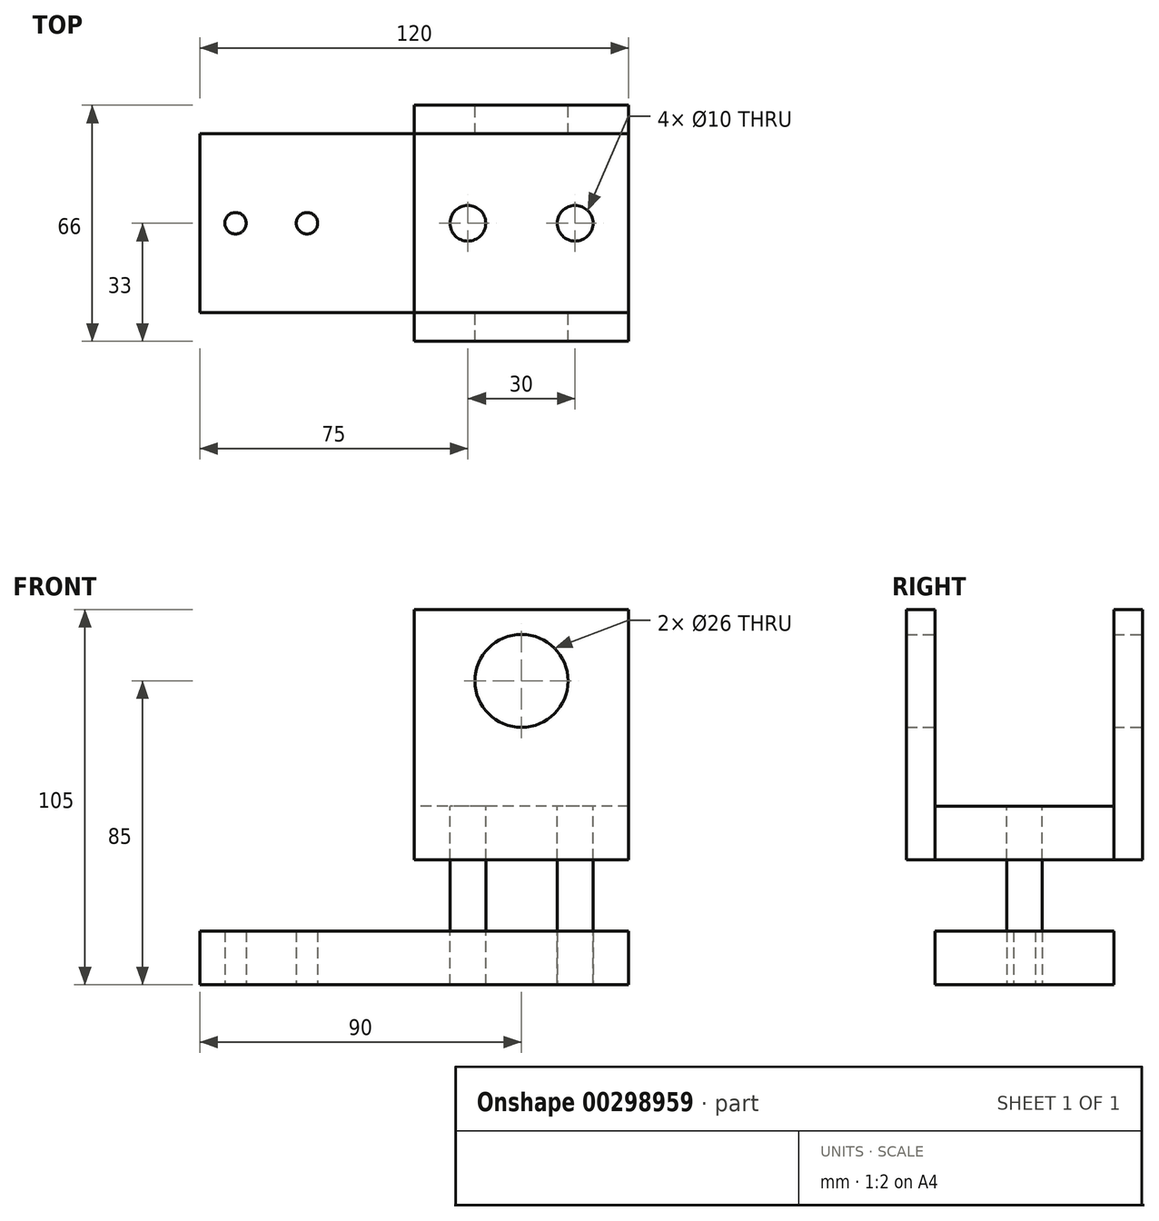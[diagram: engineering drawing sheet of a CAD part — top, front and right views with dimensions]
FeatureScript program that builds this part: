
annotation { "Feature Type Name" : "Feature", "Feature Type Description" : "" }
export const myFeature = defineFeature(function(context is Context, id is Id, definition is map)
    precondition{}
    {
        {
            var Q0;
            Q0=qCreatedBy(makeId("Top.planeOp"),FACE);
            var sketch = newSketch(context, id + "F0", { "sketchPlane" : qUnion([Q0])});
            skLineSegment(sketch, "E0.bottom", {"start": v(30, 25) * mm, "end": v(-30, 25) * mm});
            skLineSegment(sketch, "E0.top", {"start": v(30, -25) * mm, "end": v(-30, -25) * mm});
            skLineSegment(sketch, "E0.left", {"start": v(30, 25) * mm, "end": v(30, -25) * mm});
            skLineSegment(sketch, "E0.right", {"start": v(-30, 25) * mm, "end": v(-30, -25) * mm});
            skPoint(sketch, "E0.middle", {"position": v(0, 0) * mm});
            skCircle(sketch, "E1", {"center": v(15, 0) * mm, "radius": 5 * mm});
            skCircle(sketch, "E2", {"center": v(-15, 0) * mm, "radius": 5 * mm});
            skSolve(sketch);
        }
        {
            var Q0;
            Q0=makeQuery(id+"F0.imprint","IMPRINT",FACE,{"disambiguationData":[TD([[makeQuery(id+"F0.imprint","IMPRINT",EDGE,{"derivedFrom":sQuery(id+"F0.wireOp",EDGE,"E0.bottom")}),1.0]])]});
            extrude(context, id + "F1", {"entities" : qUnion([Q0]), "depth" : 15 * mm});
        }
        {
            var Q0;
            Q0=makeQuery(id+"F1.opExtrude","SWEPT_FACE",FACE,{"disambiguationData":[OSD([sQuery(id+"F0.wireOp",EDGE,"E0.top")])]});
            var sketch = newSketch(context, id + "F2", { "sketchPlane" : qUnion([Q0])});
            skLineSegment(sketch, "E3.bottom", {"start": v(-30, 0) * mm, "end": v(30, 0) * mm});
            skLineSegment(sketch, "E3.top", {"start": v(-30, 70) * mm, "end": v(30, 70) * mm});
            skLineSegment(sketch, "E3.left", {"start": v(-30, 0) * mm, "end": v(-30, 70) * mm});
            skLineSegment(sketch, "E3.right", {"start": v(30, 0) * mm, "end": v(30, 70) * mm});
            skCircle(sketch, "E4", {"center": v(0, 50) * mm, "radius": 13 * mm});
            skSolve(sketch);
        }
        {
            var Q0;
            Q0 = qSketchRegion(id + "F2", true);
            extrude(context, id + "F3", {"entities" : qUnion([Q0]), "depth" : 8 * mm});
        }
        {
            var Q0;
            Q0=makeQuery(id+"F3.opExtrude","SWEPT_BODY",BODY,{"disambiguationData":[OSD([sQuery(id+"F2.wireOp",EDGE,"E3.bottom"),sQuery(id+"F2.wireOp",EDGE,"E3.top"),sQuery(id+"F2.wireOp",EDGE,"E3.left"),sQuery(id+"F2.wireOp",EDGE,"E3.right"),sQuery(id+"F2.wireOp",EDGE,"E4")])]});
            var Q1;
            Q1=qCreatedBy(makeId("Front.planeOp"),FACE);
            transform(context, id + "F4", {"entities" : qUnion([Q0]), "transformType" : TransformType.TRANSLATION_DISTANCE, "transformDirection" : qUnion([Q1]), "distance" : 58 * mm, "oppositeDirection" : true, "makeCopy" : true});
        }
        {
            var Q0;
            Q0=makeQuery(id+"F1.opExtrude","CAP_FACE",FACE,{"disambiguationData":[OSD([sQuery(id+"F0.wireOp",EDGE,"E0.bottom"),sQuery(id+"F0.wireOp",EDGE,"E0.top"),sQuery(id+"F0.wireOp",EDGE,"E0.left"),sQuery(id+"F0.wireOp",EDGE,"E0.right"),sQuery(id+"F0.wireOp",EDGE,"E1"),sQuery(id+"F0.wireOp",EDGE,"E2")])],"isStart":false});
            var sketch = newSketch(context, id + "F5", { "sketchPlane" : qUnion([Q0])});
            skCircle(sketch, "E5", {"center": v(15, 0) * mm, "radius": 5 * mm});
            skPoint(sketch, "E5.first.point", {"position": v(10.02, 0.46) * mm});
            skPoint(sketch, "E5.second.point", {"position": v(20, 0) * mm});
            skPoint(sketch, "E5.third.point", {"position": v(14.38, -4.96) * mm});
            skCircle(sketch, "E6", {"center": v(-15, 0) * mm, "radius": 5 * mm});
            skPoint(sketch, "E6.first.point", {"position": v(-10, 0) * mm});
            skPoint(sketch, "E6.second.point", {"position": v(-20, 0) * mm});
            skPoint(sketch, "E6.third.point", {"position": v(-14.7, -5) * mm});
            skSolve(sketch);
        }
        {
            var Q0;
            Q0 = qSketchRegion(id + "F5", true);
            extrude(context, id + "F6", {"entities" : qUnion([Q0]), "oppositeDirection" : true, "depth" : 50 * mm});
        }
        {
            var Q0;
            Q0=makeQuery(id+"F6.opExtrude","CAP_FACE",FACE,{"disambiguationData":[OSD([sQuery(id+"F5.wireOp",EDGE,"E5")])],"isStart":false});
            var sketch = newSketch(context, id + "F7", { "sketchPlane" : qUnion([Q0])});
            skLineSegment(sketch, "E7.bottom", {"start": v(60, 25) * mm, "end": v(-60, 25) * mm});
            skLineSegment(sketch, "E7.top", {"start": v(60, -25) * mm, "end": v(-60, -25) * mm});
            skLineSegment(sketch, "E7.left", {"start": v(60, 25) * mm, "end": v(60, -25) * mm});
            skLineSegment(sketch, "E7.right", {"start": v(-60, 25) * mm, "end": v(-60, -25) * mm});
            skPoint(sketch, "E7.middle", {"position": v(0, 0) * mm});
            skCircle(sketch, "E8", {"center": v(45, 0) * mm, "radius": 5 * mm});
            skCircle(sketch, "E9", {"center": v(15, 0) * mm, "radius": 5 * mm});
            skCircle(sketch, "E10", {"center": v(-50, 0) * mm, "radius": 3 * mm});
            skCircle(sketch, "E11", {"center": v(-30, 0) * mm, "radius": 3 * mm});
            skSolve(sketch);
        }
        {
            var Q0;
            Q0=makeQuery(id+"F7.imprint","IMPRINT",FACE,{"disambiguationData":[TD([[makeQuery(id+"F7.imprint","IMPRINT",EDGE,{"derivedFrom":sQuery(id+"F7.wireOp",EDGE,"E7.bottom")}),1.0]])]});
            extrude(context, id + "F8", {"entities" : qUnion([Q0]), "oppositeDirection" : true, "depth" : 15 * mm});
        }
        {
            var Q0;
            Q0=makeQuery(id+"F8.opExtrude","SWEPT_BODY",BODY,{"disambiguationData":[OSD([sQuery(id+"F7.wireOp",EDGE,"E7.bottom"),sQuery(id+"F7.wireOp",EDGE,"E7.top"),sQuery(id+"F7.wireOp",EDGE,"E7.left"),sQuery(id+"F7.wireOp",EDGE,"E7.right"),sQuery(id+"F7.wireOp",EDGE,"E8"),sQuery(id+"F7.wireOp",EDGE,"E9"),sQuery(id+"F7.wireOp",EDGE,"E10"),sQuery(id+"F7.wireOp",EDGE,"E11")])]});
            transform(context, id + "F9", {"entities" : qUnion([Q0]), "transformType" : TransformType.TRANSLATION_3D, "dx" : -30 * mm, "dy" : 0 * mm, "dz" : 0 * mm, "makeCopy" : false});
        }
    });
